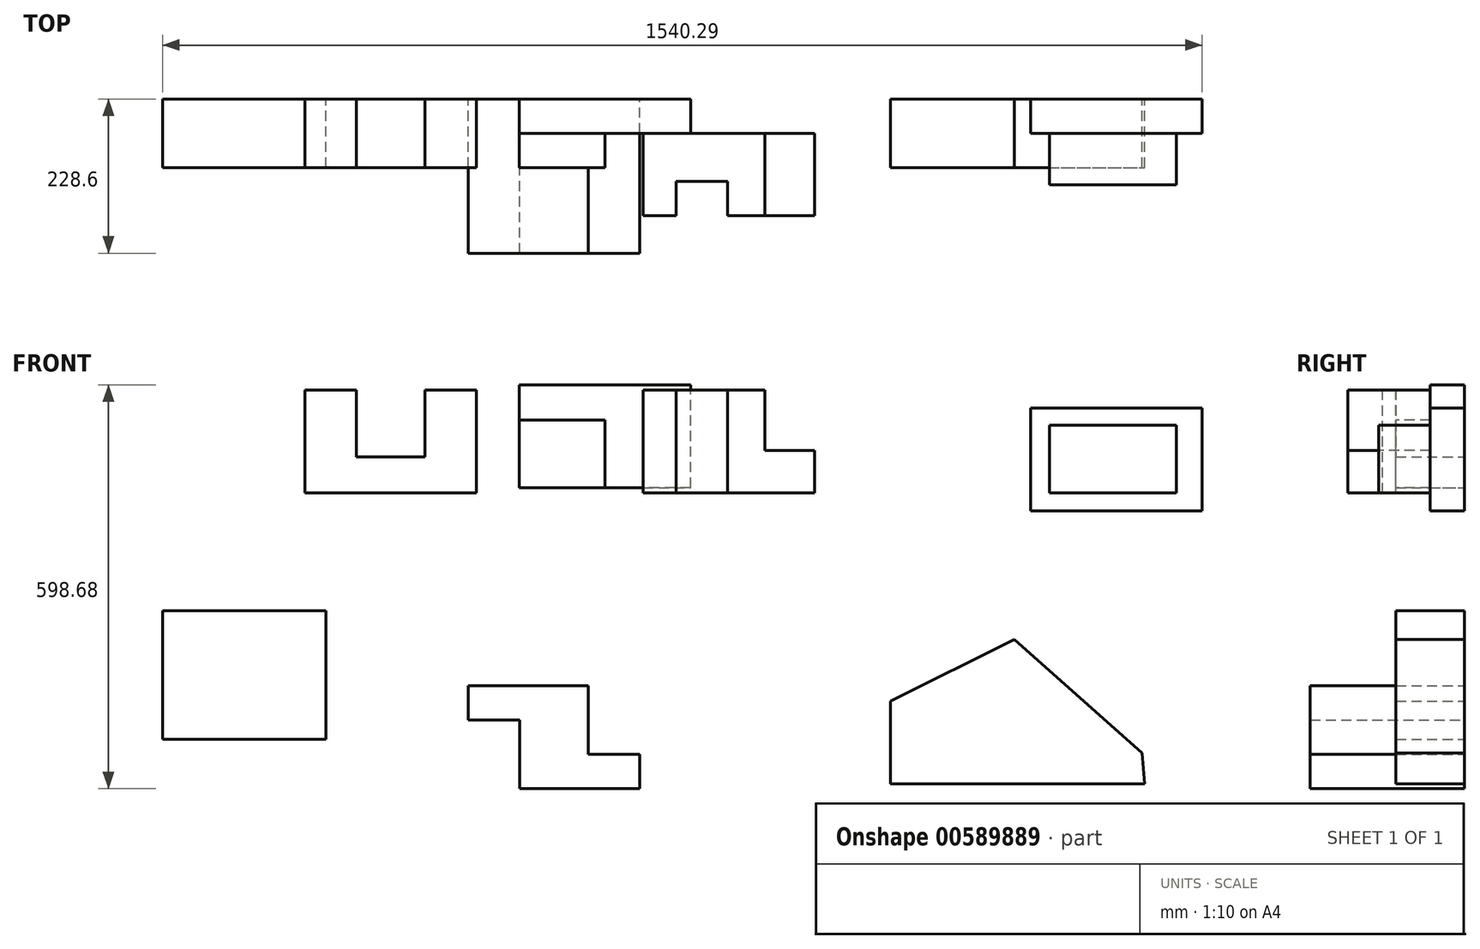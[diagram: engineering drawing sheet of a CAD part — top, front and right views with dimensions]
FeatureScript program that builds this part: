
annotation { "Feature Type Name" : "Feature", "Feature Type Description" : "" }
export const myFeature = defineFeature(function(context is Context, id is Id, definition is map)
    precondition{}
    {
        {
            var Q0;
            Q0=qCreatedBy(makeId("Front.planeOp"),FACE);
            var sketch = newSketch(context, id + "F0", { "sketchPlane" : qUnion([Q0])});
            skLineSegment(sketch, "E0", {"start": v(254, 0) * mm, "end": v(254, 152.4) * mm});
            skLineSegment(sketch, "E1", {"start": v(254, 152.4) * mm, "end": v(177.8, 152.4) * mm});
            skLineSegment(sketch, "E2", {"start": v(177.8, 152.4) * mm, "end": v(177.8, 53.07) * mm});
            skLineSegment(sketch, "E3", {"start": v(177.8, 53.07) * mm, "end": v(76.2, 53.07) * mm});
            skLineSegment(sketch, "E4", {"start": v(76.2, 53.07) * mm, "end": v(76.2, 152.4) * mm});
            skLineSegment(sketch, "E5", {"start": v(76.2, 152.4) * mm, "end": v(0, 152.4) * mm});
            skLineSegment(sketch, "E6", {"start": v(0, 152.4) * mm, "end": v(0, 0) * mm});
            skLineSegment(sketch, "E7", {"start": v(0, 0) * mm, "end": v(254, 0) * mm});
            skSolve(sketch);
        }
        {
            var Q0;
            Q0=makeQuery(id+"F0.imprint","IMPRINT",FACE,{"disambiguationData":[TD([[makeQuery(id+"F0.imprint","IMPRINT",EDGE,{"derivedFrom":sQuery(id+"F0.wireOp",EDGE,"E0")}),1.0]])]});
            extrude(context, id + "F1", {"entities" : qUnion([Q0]), "depth" : 101.6 * mm, "offsetDistance" : 25.4 * mm});
        }
        {
            var Q0;
            Q0=qCreatedBy(makeId("Front.planeOp"),FACE);
            var sketch = newSketch(context, id + "F2", { "sketchPlane" : qUnion([Q0])});
            skLineSegment(sketch, "E8.bottom", {"start": v(317.16, 7.63) * mm, "end": v(571.16, 7.63) * mm});
            skLineSegment(sketch, "E8.top", {"start": v(317.16, 160.03) * mm, "end": v(571.16, 160.03) * mm});
            skLineSegment(sketch, "E8.left", {"start": v(317.16, 7.63) * mm, "end": v(317.16, 160.03) * mm});
            skLineSegment(sketch, "E8.right", {"start": v(571.16, 7.63) * mm, "end": v(571.16, 160.03) * mm});
            skSolve(sketch);
        }
        {
            var Q0;
            Q0=makeQuery(id+"F2.imprint","IMPRINT",FACE,{"disambiguationData":[TD([[makeQuery(id+"F2.imprint","IMPRINT",EDGE,{"derivedFrom":sQuery(id+"F2.wireOp",EDGE,"E8.bottom")}),1.0]])]});
            extrude(context, id + "F3", {"entities" : qUnion([Q0]), "depth" : 101.6 * mm, "offsetDistance" : 25.4 * mm});
        }
        {
            var Q0;
            Q0=makeQuery(id+"F3.opExtrude","SWEPT_FACE",FACE,{"disambiguationData":[OSD([sQuery(id+"F2.wireOp",EDGE,"E8.top")])]});
            var sketch = newSketch(context, id + "F4", { "sketchPlane" : qUnion([Q0])});
            skLineSegment(sketch, "E9.bottom", {"start": v(571.16, -50.8) * mm, "end": v(444.16, -50.8) * mm});
            skLineSegment(sketch, "E9.top", {"start": v(571.16, -101.6) * mm, "end": v(444.16, -101.6) * mm});
            skLineSegment(sketch, "E9.left", {"start": v(571.16, -50.8) * mm, "end": v(571.16, -101.6) * mm});
            skLineSegment(sketch, "E9.right", {"start": v(444.16, -50.8) * mm, "end": v(444.16, -101.6) * mm});
            skSolve(sketch);
        }
        {
            var Q0;
            Q0=makeQuery(id+"F4.imprint","IMPRINT",FACE,{"disambiguationData":[TD([[makeQuery(id+"F4.imprint","IMPRINT",EDGE,{"derivedFrom":sQuery(id+"F4.wireOp",EDGE,"E9.bottom")}),1.0]])]});
            extrude(context, id + "F5", {"entities" : qUnion([Q0]), "operationType" : NewBodyOperationType.REMOVE, "oppositeDirection" : true, "depth" : 152.4 * mm, "offsetDistance" : 25.4 * mm});
        }
        {
            var Q0;
            Q0=makeQuery(id+"F3.opExtrude","CAP_FACE",FACE,{"disambiguationData":[OSD([sQuery(id+"F2.wireOp",EDGE,"E8.bottom"),sQuery(id+"F2.wireOp",EDGE,"E8.top"),sQuery(id+"F2.wireOp",EDGE,"E8.left"),sQuery(id+"F2.wireOp",EDGE,"E8.right")])],"isStart":false});
            var sketch = newSketch(context, id + "F6", { "sketchPlane" : qUnion([Q0])});
            skLineSegment(sketch, "E10.bottom", {"start": v(317.16, 160.03) * mm, "end": v(444.16, 160.03) * mm});
            skLineSegment(sketch, "E10.top", {"start": v(317.16, 107.58) * mm, "end": v(444.16, 107.58) * mm});
            skLineSegment(sketch, "E10.left", {"start": v(317.16, 160.03) * mm, "end": v(317.16, 107.58) * mm});
            skLineSegment(sketch, "E10.right", {"start": v(444.16, 160.03) * mm, "end": v(444.16, 107.58) * mm});
            skSolve(sketch);
        }
        {
            var Q0;
            Q0=makeQuery(id+"F6.imprint","IMPRINT",FACE,{"disambiguationData":[TD([[makeQuery(id+"F6.imprint","IMPRINT",EDGE,{"derivedFrom":sQuery(id+"F6.wireOp",EDGE,"E10.bottom")}),-1.0]])]});
            extrude(context, id + "F7", {"entities" : qUnion([Q0]), "operationType" : NewBodyOperationType.REMOVE, "oppositeDirection" : true, "depth" : 50.8 * mm, "offsetDistance" : 25.4 * mm});
        }
        {
            var Q0;
            Q0=makeQuery(id+"F7.boolean.opBoolean","MERGE",FACE,{"derivedFrom":[makeQuery(id+"F5.boolean.opBoolean","COPY",FACE,{"derivedFrom":makeQuery(id+"F5.opExtrude","SWEPT_FACE",FACE,{"disambiguationData":[OSD([sQuery(id+"F4.wireOp",EDGE,"E9.bottom")])]})}),makeQuery(id+"F7.opExtrude","CAP_FACE",FACE,{"disambiguationData":[OSD([sQuery(id+"F6.wireOp",EDGE,"E10.bottom"),sQuery(id+"F6.wireOp",EDGE,"E10.top"),sQuery(id+"F6.wireOp",EDGE,"E10.left"),sQuery(id+"F6.wireOp",EDGE,"E10.right")])],"isStart":false})]});
            var sketch = newSketch(context, id + "F8", { "sketchPlane" : qUnion([Q0])});
            skLineSegment(sketch, "E11.bottom", {"start": v(500.85, 152.4) * mm, "end": v(754.85, 152.4) * mm});
            skLineSegment(sketch, "E11.top", {"start": v(500.85, 0) * mm, "end": v(754.85, 0) * mm});
            skLineSegment(sketch, "E11.left", {"start": v(500.85, 152.4) * mm, "end": v(500.85, 0) * mm});
            skLineSegment(sketch, "E11.right", {"start": v(754.85, 152.4) * mm, "end": v(754.85, 0) * mm});
            skSolve(sketch);
        }
        {
            var Q0;
            Q0=qSketchRegion(id+"F8",true);
            extrude(context, id + "F9", {"entities" : qUnion([Q0]), "operationType" : NewBodyOperationType.ADD, "depth" : 121.92 * mm, "offsetDistance" : 25.4 * mm});
        }
        {
            var Q0;
            Q0=makeQuery(id+"F9.opExtrude","CAP_FACE",FACE,{"disambiguationData":[OSD([sQuery(id+"F8.wireOp",EDGE,"E11.bottom"),sQuery(id+"F8.wireOp",EDGE,"E11.top"),sQuery(id+"F8.wireOp",EDGE,"E11.left"),sQuery(id+"F8.wireOp",EDGE,"E11.right")])],"isStart":false});
            var sketch = newSketch(context, id + "F10", { "sketchPlane" : qUnion([Q0])});
            skLineSegment(sketch, "E12.bottom", {"start": v(551.65, 152.4) * mm, "end": v(500.85, 152.4) * mm});
            skLineSegment(sketch, "E12.top", {"start": v(551.65, 0) * mm, "end": v(500.85, 0) * mm});
            skLineSegment(sketch, "E12.left", {"start": v(551.65, 152.4) * mm, "end": v(551.65, 0) * mm});
            skLineSegment(sketch, "E12.right", {"start": v(500.85, 152.4) * mm, "end": v(500.85, 0) * mm});
            skSolve(sketch);
        }
        {
            var Q0;
            {var subQ0=sQuery(id+"F10.wireOp",EDGE,"E12.left");Q0=makeQuery(id+"F10.imprint","IMPRINT",FACE,{"disambiguationData":[TD([[makeQuery(id+"F10.imprint","IMPRINT",EDGE,{"derivedFrom":subQ0}),1.0]])]});}
            var sketch = newSketch(context, id + "F11", { "sketchPlane" : qUnion([Q0])});
            skLineSegment(sketch, "E13.bottom", {"start": v(757.59, 164.43) * mm, "end": v(681.39, 164.43) * mm});
            skLineSegment(sketch, "E13.top", {"start": v(757.59, 62.83) * mm, "end": v(681.39, 62.83) * mm});
            skLineSegment(sketch, "E13.left", {"start": v(757.59, 164.43) * mm, "end": v(757.59, 62.83) * mm});
            skLineSegment(sketch, "E13.right", {"start": v(681.39, 164.43) * mm, "end": v(681.39, 62.83) * mm});
            skSolve(sketch);
        }
        {
            var Q0;
            Q0=qSketchRegion(id+"F11",true);
            extrude(context, id + "F12", {"entities" : qUnion([Q0]), "operationType" : NewBodyOperationType.REMOVE, "oppositeDirection" : true, "depth" : 152.4 * mm, "offsetDistance" : 25.4 * mm});
        }
        {
            var Q0;
            {var subQ0=sQuery(id+"F10.wireOp",EDGE,"E12.left");Q0=makeQuery(id+"F10.imprint","IMPRINT",FACE,{"disambiguationData":[TD([[makeQuery(id+"F10.imprint","IMPRINT",EDGE,{"derivedFrom":subQ0}),1.0]])]});}
            var sketch = newSketch(context, id + "F13", { "sketchPlane" : qUnion([Q0])});
            skSolve(sketch);
        }
        {
            var Q0;
            Q0=qCreatedBy(makeId("Front.planeOp"),FACE);
            var sketch = newSketch(context, id + "F14", { "sketchPlane" : qUnion([Q0])});
            skLineSegment(sketch, "E14.bottom", {"start": v(-211.06, -175.13) * mm, "end": v(31.18, -175.13) * mm});
            skLineSegment(sketch, "E14.top", {"start": v(-211.06, -365.46) * mm, "end": v(31.18, -365.46) * mm});
            skLineSegment(sketch, "E14.left", {"start": v(-211.06, -175.13) * mm, "end": v(-211.06, -365.46) * mm});
            skLineSegment(sketch, "E14.right", {"start": v(31.18, -175.13) * mm, "end": v(31.18, -365.46) * mm});
            skSolve(sketch);
        }
        {
            var Q0;
            Q0=qSketchRegion(id+"F14",true);
            extrude(context, id + "F15", {"entities" : qUnion([Q0]), "depth" : 101.6 * mm, "offsetDistance" : 25.4 * mm});
        }
        {
            var Q0;
            Q0=qCreatedBy(makeId("Front.planeOp"),FACE);
            var sketch = newSketch(context, id + "F16", { "sketchPlane" : qUnion([Q0])});
            skLineSegment(sketch, "E15", {"start": v(242.02, -286.25) * mm, "end": v(419.82, -286.25) * mm});
            skLineSegment(sketch, "E16", {"start": v(419.82, -286.25) * mm, "end": v(419.82, -387.85) * mm});
            skLineSegment(sketch, "E17", {"start": v(419.82, -387.85) * mm, "end": v(496.02, -387.85) * mm});
            skLineSegment(sketch, "E18", {"start": v(496.02, -387.85) * mm, "end": v(496.02, -438.65) * mm});
            skLineSegment(sketch, "E19", {"start": v(242.02, -286.25) * mm, "end": v(242.02, -337.05) * mm});
            skLineSegment(sketch, "E20", {"start": v(242.02, -337.05) * mm, "end": v(318.22, -337.05) * mm});
            skLineSegment(sketch, "E21", {"start": v(318.22, -337.05) * mm, "end": v(318.22, -438.65) * mm});
            skLineSegment(sketch, "E22", {"start": v(318.22, -438.65) * mm, "end": v(496.02, -438.65) * mm});
            skSolve(sketch);
        }
        {
            var Q0;
            Q0=makeQuery(id+"F16.imprint","IMPRINT",FACE,{"disambiguationData":[TD([[makeQuery(id+"F16.imprint","IMPRINT",EDGE,{"derivedFrom":sQuery(id+"F16.wireOp",EDGE,"E15")}),-1.0]])]});
            extrude(context, id + "F17", {"entities" : qUnion([Q0]), "depth" : 101.6 * mm, "offsetDistance" : 25.4 * mm});
        }
        {
            var Q0;
            Q0=makeQuery(id+"F17.opExtrude","CAP_FACE",FACE,{"disambiguationData":[OSD([sQuery(id+"F16.wireOp",EDGE,"E15"),sQuery(id+"F16.wireOp",EDGE,"E16"),sQuery(id+"F16.wireOp",EDGE,"E17"),sQuery(id+"F16.wireOp",EDGE,"E18"),sQuery(id+"F16.wireOp",EDGE,"E19"),sQuery(id+"F16.wireOp",EDGE,"E20"),sQuery(id+"F16.wireOp",EDGE,"E21"),sQuery(id+"F16.wireOp",EDGE,"E22")])],"isStart":false});
            var sketch = newSketch(context, id + "F18", { "sketchPlane" : qUnion([Q0])});
            skSolve(sketch);
        }
        {
            var Q0;
            Q0=makeQuery(id+"F18.imprint","IMPRINT",FACE,{"disambiguationData":[TD([[makeQuery(id+"F18.imprint","IMPRINT",EDGE,{"derivedFrom":makeQuery(id+"F17.opExtrude","CAP_EDGE",EDGE,{"disambiguationData":[OSD([sQuery(id+"F16.wireOp",EDGE,"E15")])],"isStart":false})}),-1.0]])]});
            var sketch = newSketch(context, id + "F19", { "sketchPlane" : qUnion([Q0])});
            skSolve(sketch);
        }
        {
            var Q0;
            Q0=makeQuery(id+"F19.imprint","IMPRINT",FACE,{"disambiguationData":[TD([[makeQuery(id+"F19.imprint","IMPRINT",EDGE,{"derivedFrom":makeQuery(id+"F18.imprint","IMPRINT",EDGE,{"derivedFrom":makeQuery(id+"F17.opExtrude","CAP_EDGE",EDGE,{"disambiguationData":[OSD([sQuery(id+"F16.wireOp",EDGE,"E15")])],"isStart":false})})}),-1.0]])]});
            var Q1;
            Q1=makeQuery(id+"F18.imprint","IMPRINT",FACE,{"disambiguationData":[TD([[makeQuery(id+"F18.imprint","IMPRINT",EDGE,{"derivedFrom":makeQuery(id+"F17.opExtrude","CAP_EDGE",EDGE,{"disambiguationData":[OSD([sQuery(id+"F16.wireOp",EDGE,"E15")])],"isStart":false})}),-1.0]])]});
            var Q2;
            Q2=makeQuery(id+"F17.opExtrude","CAP_FACE",FACE,{"disambiguationData":[OSD([sQuery(id+"F16.wireOp",EDGE,"E15"),sQuery(id+"F16.wireOp",EDGE,"E16"),sQuery(id+"F16.wireOp",EDGE,"E17"),sQuery(id+"F16.wireOp",EDGE,"E18"),sQuery(id+"F16.wireOp",EDGE,"E19"),sQuery(id+"F16.wireOp",EDGE,"E20"),sQuery(id+"F16.wireOp",EDGE,"E21"),sQuery(id+"F16.wireOp",EDGE,"E22")])],"isStart":false});
            var Q3;
            Q3=makeQuery(id+"F17.opExtrude","CAP_FACE",FACE,{"disambiguationData":[OSD([sQuery(id+"F16.wireOp",EDGE,"E15"),sQuery(id+"F16.wireOp",EDGE,"E16"),sQuery(id+"F16.wireOp",EDGE,"E17"),sQuery(id+"F16.wireOp",EDGE,"E18"),sQuery(id+"F16.wireOp",EDGE,"E19"),sQuery(id+"F16.wireOp",EDGE,"E20"),sQuery(id+"F16.wireOp",EDGE,"E21"),sQuery(id+"F16.wireOp",EDGE,"E22")])],"isStart":true});
            extrude(context, id + "F20", {"entities" : qUnion([Q0, Q1, Q2, Q3]), "operationType" : NewBodyOperationType.ADD, "depth" : 127 * mm, "offsetDistance" : 25.4 * mm});
        }
        {
            var Q0;
            Q0=qCreatedBy(makeId("Front.planeOp"),FACE);
            var sketch = newSketch(context, id + "F21", { "sketchPlane" : qUnion([Q0])});
            skLineSegment(sketch, "E23", {"start": v(867.45, -431.57) * mm, "end": v(1244.14, -431.57) * mm});
            skLineSegment(sketch, "E24", {"start": v(867.45, -431.57) * mm, "end": v(867.45, -308.9) * mm});
            skLineSegment(sketch, "E25", {"start": v(867.45, -308.9) * mm, "end": v(1050.84, -217.2) * mm});
            skLineSegment(sketch, "E26", {"start": v(1050.84, -217.2) * mm, "end": v(1240.43, -385.72) * mm});
            skLineSegment(sketch, "E27", {"start": v(1240.43, -385.72) * mm, "end": v(1244.14, -431.57) * mm});
            skSolve(sketch);
        }
        {
            var Q0;
            Q0=qCreatedBy(makeId("Front.planeOp"),FACE);
            var sketch = newSketch(context, id + "F22", { "sketchPlane" : qUnion([Q0])});
            skLineSegment(sketch, "E28.bottom", {"start": v(1075.23, 125.37) * mm, "end": v(1329.23, 125.37) * mm});
            skLineSegment(sketch, "E28.top", {"start": v(1075.23, -27.03) * mm, "end": v(1329.23, -27.03) * mm});
            skLineSegment(sketch, "E28.left", {"start": v(1075.23, 125.37) * mm, "end": v(1075.23, -27.03) * mm});
            skLineSegment(sketch, "E28.right", {"start": v(1329.23, 125.37) * mm, "end": v(1329.23, -27.03) * mm});
            skSolve(sketch);
        }
        {
            var Q0;
            Q0=makeQuery(id+"F22.imprint","IMPRINT",FACE,{"disambiguationData":[TD([[makeQuery(id+"F22.imprint","IMPRINT",EDGE,{"derivedFrom":sQuery(id+"F22.wireOp",EDGE,"E28.bottom")}),-1.0]])]});
            extrude(context, id + "F23", {"entities" : qUnion([Q0]), "depth" : 50.8 * mm, "offsetDistance" : 25.4 * mm});
        }
        {
            var Q0;
            Q0=makeQuery(id+"F21.imprint","IMPRINT",FACE,{"disambiguationData":[TD([[makeQuery(id+"F21.imprint","IMPRINT",EDGE,{"derivedFrom":sQuery(id+"F21.wireOp",EDGE,"E23")}),1.0]])]});
            extrude(context, id + "F24", {"entities" : qUnion([Q0]), "depth" : 101.6 * mm, "offsetDistance" : 25.4 * mm});
        }
        {
            var Q0;
            Q0=makeQuery(id+"F24.opExtrude","CAP_FACE",FACE,{"disambiguationData":[OSD([sQuery(id+"F21.wireOp",EDGE,"E23"),sQuery(id+"F21.wireOp",EDGE,"E24"),sQuery(id+"F21.wireOp",EDGE,"E25"),sQuery(id+"F21.wireOp",EDGE,"E26"),sQuery(id+"F21.wireOp",EDGE,"E27")])],"isStart":false});
            var sketch = newSketch(context, id + "F25", { "sketchPlane" : qUnion([Q0])});
            skSolve(sketch);
        }
        {
            var Q0;
            Q0=makeQuery(id+"F23.opExtrude","CAP_FACE",FACE,{"disambiguationData":[OSD([sQuery(id+"F22.wireOp",EDGE,"E28.bottom"),sQuery(id+"F22.wireOp",EDGE,"E28.top"),sQuery(id+"F22.wireOp",EDGE,"E28.left"),sQuery(id+"F22.wireOp",EDGE,"E28.right")])],"isStart":false});
            var sketch = newSketch(context, id + "F26", { "sketchPlane" : qUnion([Q0])});
            skSolve(sketch);
        }
        {
            var Q0;
            Q0=makeQuery(id+"F26.imprint","IMPRINT",FACE,{"disambiguationData":[TD([[makeQuery(id+"F26.imprint","IMPRINT",EDGE,{"derivedFrom":makeQuery(id+"F23.opExtrude","CAP_EDGE",EDGE,{"disambiguationData":[OSD([sQuery(id+"F22.wireOp",EDGE,"E28.bottom")])],"isStart":false})}),-1.0]])]});
            var sketch = newSketch(context, id + "F27", { "sketchPlane" : qUnion([Q0])});
            skLineSegment(sketch, "E29.bottom", {"start": v(1102.85, 99.9) * mm, "end": v(1290.78, 99.9) * mm});
            skLineSegment(sketch, "E29.top", {"start": v(1102.85, 0) * mm, "end": v(1290.78, 0) * mm});
            skLineSegment(sketch, "E29.left", {"start": v(1102.85, 99.9) * mm, "end": v(1102.85, 0) * mm});
            skLineSegment(sketch, "E29.right", {"start": v(1290.78, 99.9) * mm, "end": v(1290.78, 0) * mm});
            skSolve(sketch);
        }
        {
            var Q0;
            Q0=qSketchRegion(id+"F27",true);
            extrude(context, id + "F28", {"entities" : qUnion([Q0]), "operationType" : NewBodyOperationType.ADD, "depth" : 76.2 * mm, "offsetDistance" : 25.4 * mm});
        }
        {
            var Q0;
            {var subQ0=sQuery(id+"F10.wireOp",EDGE,"E12.left");Q0=makeQuery(id+"F13.imprint","IMPRINT",FACE,{"disambiguationData":[TD([[makeQuery(id+"F13.imprint","IMPRINT",EDGE,{"derivedFrom":makeQuery(id+"F10.imprint","IMPRINT",EDGE,{"derivedFrom":subQ0})}),1.0]])]});}
            var sketch = newSketch(context, id + "F29", { "sketchPlane" : qUnion([Q0])});
            skLineSegment(sketch, "E30.bottom", {"start": v(550.05, 153.44) * mm, "end": v(626.25, 153.44) * mm});
            skLineSegment(sketch, "E30.top", {"start": v(550.05, 0) * mm, "end": v(626.25, 0) * mm});
            skLineSegment(sketch, "E30.left", {"start": v(550.05, 153.44) * mm, "end": v(550.05, 0) * mm});
            skLineSegment(sketch, "E30.right", {"start": v(626.25, 153.44) * mm, "end": v(626.25, 0) * mm});
            skSolve(sketch);
        }
        {
            var Q0;
            Q0=qSketchRegion(id+"F29",true);
            extrude(context, id + "F30", {"entities" : qUnion([Q0]), "operationType" : NewBodyOperationType.REMOVE, "oppositeDirection" : true, "depth" : 50.8 * mm, "offsetDistance" : 25.4 * mm});
        }
    });
